# Revit family: Haworth_XSeries_ComboUnit_2HighOpenShelf
name_source: partatom
category: Furniture Systems
units: mm (PartAtom-declared; Revit-internal decimal feet)

## family parameters
Always vertical = Yes
Cut with Voids When Loaded = No
OmniClass Number = 23.40.70.14.64.21
OmniClass Title = Systems Furniture
Part Type = Normal
Room Calculation Point = No
Round Connector Dimension = Use Diameter
Shared = No
Work Plane-Based = No

## types (1)
- 18d 30w 27h
    Actual Depth = 18 3/4"
    Actual Height = 27 1/2"
    Actual Width = 29 7/8"
    Assembly Code = E2020200
    Cabinet Height = 27 1/2"
    Classic Pull = No
    Crescent Pull = No
    Custom Size = No
    Description = Haworth XSeries Combo Unit - Open Shelf - 18d 30w 27h
    Drawer Height = 12 3/16"
    Drawer Width = 29 7/8"
    Ellipse Pull = No
    J Pull = No
    Linear Pull = Yes
    Manufacturer = Haworth
    Max. Height = 27 1/2"
    Max. Width = 41 7/8"
    Min. Height = 27 1/2"
    Min. Width = 29 7/8"
    Model = JCPZ
    Pull Finish = Haworth _ Metal _ Brushed Aluminum
    Radius Pull = No
    Revision Number = 5
    Size = Verify Final Dim. w/ Haworth
    Standard Widths = 30 in.
    Sustainability Info = https://www.haworth.com
    Taper Pull = No
    URL = http://www.haworth.com
    URL - Product = https://www.haworth.com
    Warranty = https://cdn.shopify.com
    Width = 30"

## geometry (parser evidence)
native form markers: Sweep x6
no freeform markers — native parametric forms only
